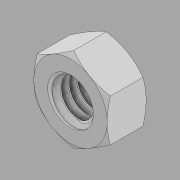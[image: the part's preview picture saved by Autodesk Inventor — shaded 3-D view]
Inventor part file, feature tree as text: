
AUTODESK INVENTOR PART (.ipt)
format: ipt  version: 2020 (Build 240168000, 168)  size: 298,496 bytes
history: native  units: in
note: dims shown in document units (in); Inventor stores cm internally (conversion verified against a paired STEP export)
features: mirror x1
ambient origin geometry x8: Origin, YZ Plane, XZ Plane, XY Plane, X Axis, Y Axis, Z Axis, Center Point
bodies: Solid1 (feature_tree)
feature tree (1):
  mirror  "Mirror1"
